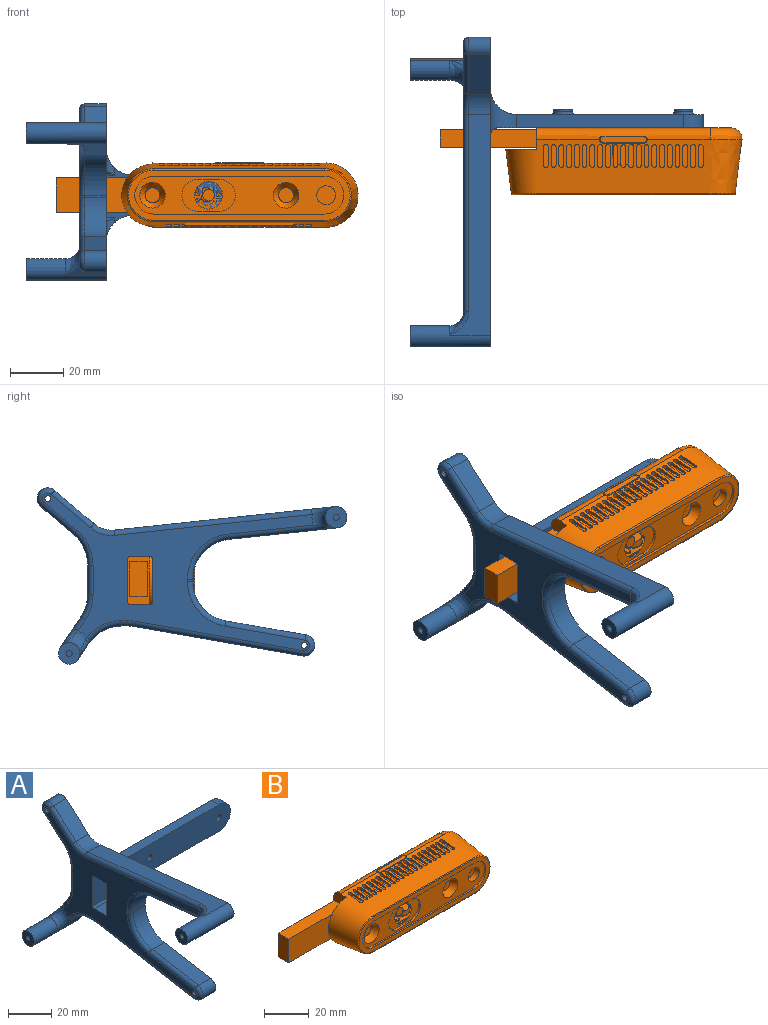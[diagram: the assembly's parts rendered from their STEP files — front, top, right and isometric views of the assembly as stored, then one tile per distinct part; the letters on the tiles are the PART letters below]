
ASSEMBLY  parts=2 mates=1
PART A: 85 faces, bbox 112.3x118.8x72.5 mm
  f0: plane 26.04x23.75mm, normal (1,0,0), area 153.5mm2, adj f2,f3,f4,f35,f36,f37,f38
  f1: plane 8x2.06mm, normal (0,0,-1), area 16.5mm2, adj f36,f37,f39,f75
  f2: plane 15.08x5.93mm, normal (0,-0.83,-0.56), area 75.7mm2, adj f0,f3,f37,f72
  f3: cylinder r=4mm len=30mm, axis (1,0,0), area 377mm2, adj f0,f2,f4,f48,f49
  f4: plane 15.08x11.42mm, normal (0,0.83,0.56), area 128.8mm2, adj f0,f3,f38,f70,f71
  f5: plane 11.07x8mm, normal (0,1,0), area 88.6mm2, adj f35,f38,f41,f68
  f6: plane 12.25x10.4mm, normal (0,0.65,-0.76), area 128.6mm2, adj f7,f21,f41,f66
  f7: cylinder r=4mm len=8mm, axis (1,0,0), area 100.5mm2, adj f6,f8,f21,f65
  f8: plane 14.75x12.52mm, normal (0,-0.65,0.76), area 154.8mm2, adj f7,f21,f60,f64
  f9: plane 85.19x17.55mm, normal (0,0.11,0.99), area 684mm2, adj f10,f21,f60,f61,f62
  f10: cylinder r=4mm len=30mm, axis (1,0,0), area 564.5mm2, adj f9,f11,f21,f47,f58
  f11: plane 40.7x15.08mm, normal (0,-0.11,-0.99), area 346mm2, adj f10,f21,f42,f83,f84
  f12: plane 8x0.82mm, normal (0,-1,0), area 6.6mm2, adj f21,f40,f42,f81
  f13: plane 29.98x8mm, normal (0,-0.17,0.99), area 243.5mm2, adj f14,f21,f40,f79
  f14: cylinder r=4mm len=8mm, axis (1,0,0), area 100.5mm2, adj f13,f19,f21,f78
  f15: plane 10.76x7.35mm, normal (0,0,-1), area 74mm2, adj f20,f21,f44,f56,f57
  f16: plane 89.86x20.72mm, normal (0,-1,0), area 1330mm2, adj f20,f22,f24,f25,f26,f30,f34,f36
  f17: plane 10.76x7.35mm, normal (0,0,1), area 74mm2, adj f20,f21,f43,f54,f55
  f18: plane 16x10mm, normal (0,1,0), area 160mm2, adj f20,f21,f55,f56
  f19: plane 62.91x11.02mm, normal (0,0.17,-0.99), area 511mm2, adj f14,f21,f39,f77
  f20: plane 101.4x59mm, normal (-1,0,0), area 1644.5mm2, adj f15,f16,f17,f18,f45,f46,f54,f55
  f21: plane 116x63mm, normal (1,0,0), area 1845mm2, adj f6,f7,f8,f9,f10,f11,f12,f13
  f22: plane 62.36x5mm, normal (0,0,1), area 311.8mm2, adj f16,f23,f24,f34
  f23: plane 69.86x15mm, normal (0,1,0), area 896.6mm2, adj f22,f24,f25,f32,f33,f35
  f24: cylinder r=7.5mm len=15mm, axis (0,1,0), area 117.8mm2, adj f16,f22,f23,f25
  f25: plane 62.36x5mm, normal (0,0,-1), area 311.8mm2, adj f16,f23,f24,f36
  f26: cylinder r=1.75mm len=7mm, axis (0,-1,0), area 77mm2, adj f16,f28
  f27: cylinder r=3.5mm len=7mm, axis (0,-1,0), area 22mm2, adj f28,f33
  f28: plane 7x7mm, normal (0,1,0), area 28.9mm2, adj f26,f27
  f29: cylinder r=3.5mm len=7mm, axis (0,-1,0), area 22mm2, adj f31,f32
  f30: cylinder r=1.75mm len=7mm, axis (0,-1,0), area 77mm2, adj f16,f31
  f31: plane 7x7mm, normal (0,1,0), area 28.9mm2, adj f29,f30
  f32: torus R=4.5mm, axis (0,1,0), area 38.1mm2, adj f23,f29
  f33: torus R=4.5mm, axis (0,1,0), area 38.1mm2, adj f23,f27
  f34: cylinder r=10mm len=18mm, axis (0,-1,0), area 169mm2, adj f16,f21,f22,f35,f44
  f35: cylinder r=10mm len=35mm, axis (0,0,1), area 392.7mm2, adj f0,f5,f21,f23,f34,f36
  f36: cylinder r=10mm len=18mm, axis (0,1,0), area 147.6mm2, adj f0,f1,f16,f21,f25,f35,f43
  f37: cylinder r=15mm len=12.44mm, axis (-1,0,0), area 117.4mm2, adj f0,f1,f2,f73,f74
  f38: cylinder r=15mm len=8.39mm, axis (-1,0,0), area 71.2mm2, adj f0,f4,f5,f69
  f39: cylinder r=15mm len=8mm, axis (-1,0,0), area 20.8mm2, adj f1,f19,f21,f76
  f40: cylinder r=15mm len=14.78mm, axis (1,0,0), area 167.7mm2, adj f12,f13,f21,f80
  f41: cylinder r=15mm len=11.43mm, axis (-1,0,0), area 104mm2, adj f5,f6,f21,f67
  f42: cylinder r=15mm len=14.92mm, axis (-1,0,0), area 175.8mm2, adj f11,f12,f21,f82
  f43: cylinder r=3mm len=9mm, axis (0,0,-1), area 22.1mm2, adj f16,f17,f21,f36,f54
  f44: cylinder r=3mm len=10mm, axis (0,0,-1), area 26.8mm2, adj f15,f16,f21,f34,f57
  f45: cylinder r=1.15mm len=10mm, axis (-1,0,0), area 72.3mm2, adj f20,f21
  f46: cylinder r=1.15mm len=10mm, axis (-1,0,0), area 72.3mm2, adj f20,f21
  f47: plane 8x8mm, normal (-1,0,0), area 46.1mm2, adj f10,f52
  f48: extruded ~14.92x7.32mm, area 187.5mm2, adj f3,f49,f59
  f49: plane 8x8mm, normal (-1,0,0), area 46.1mm2, adj f3,f48,f50
  f50: cylinder r=1.15mm len=7mm, axis (-1,0,0), area 50.6mm2, adj f49,f51
  f51: plane 2.3x2.3mm, normal (-1,0,0), area 4.2mm2, adj f50
  f52: cylinder r=1.15mm len=7mm, axis (-1,0,0), area 50.6mm2, adj f47,f53
  f53: plane 2.3x2.3mm, normal (-1,0,0), area 4.2mm2, adj f52
  f54: cylinder r=1mm len=13mm, axis (1,0,0), area 18.7mm2, adj f16,f17,f20,f43
  f55: cylinder r=1mm len=10mm, axis (-1,0,0), area 15.7mm2, adj f17,f18,f20,f21
  f56: cylinder r=1mm len=10mm, axis (-1,0,0), area 15.7mm2, adj f15,f18,f20,f21
  f57: cylinder r=1mm len=13mm, axis (1,0,0), area 18.7mm2, adj f15,f16,f20,f44
  f58: torus R=9.08mm, axis (1,0,0), area 51.8mm2, adj f10,f20,f61,f84
  f59: bspline ~16.86x14.51mm, area 51.9mm2, adj f20,f48,f71,f72,f73
  f60: cylinder r=10mm len=8mm, axis (-1,0,0), area 64.8mm2, adj f8,f9,f21,f63
  f61: bspline ~10.33x7.08mm, area 13.1mm2, adj f9,f58,f62
  f62: cylinder r=2mm len=74.12mm, axis (0,0.99,-0.11), area 233.5mm2, adj f9,f20,f61,f63
  f63: torus R=12mm, axis (1,0,0), area 27.3mm2, adj f20,f60,f62,f64
  f64: cylinder r=2mm len=16.04mm, axis (0,0.76,0.65), area 60.8mm2, adj f8,f20,f63,f65
  f65: torus R=2mm, axis (1,0,0), area 32.3mm2, adj f7,f20,f64,f66
  f66: cylinder r=2mm len=13.54mm, axis (0,-0.76,-0.65), area 50.5mm2, adj f6,f20,f65,f67
  f67: torus R=17mm, axis (1,0,0), area 42.8mm2, adj f20,f41,f66,f68
  f68: cylinder r=2mm len=11.07mm, axis (0,0,-1), area 34.8mm2, adj f5,f20,f67,f69
  f69: torus R=17mm, axis (1,0,0), area 29.3mm2, adj f20,f38,f68,f70
  f70: cylinder r=2mm len=5.19mm, axis (0,0.56,-0.83), area 15.4mm2, adj f4,f20,f69,f71
  f71: bspline ~8.69x7.34mm, area 22.2mm2, adj f4,f59,f70
  f72: bspline ~8.43x7.09mm, area 17.8mm2, adj f2,f59,f73
  f73: bspline ~3.5x3.18mm, area 4mm2, adj f37,f59,f72,f74
  f74: torus R=17mm, axis (1,0,0), area 43.4mm2, adj f20,f37,f73,f75
  f75: cylinder r=2mm len=2.06mm, axis (0,-1,0), area 6.5mm2, adj f1,f20,f74,f76
  f76: torus R=17mm, axis (1,0,0), area 8.6mm2, adj f20,f39,f75,f77
  f77: cylinder r=2mm len=63.26mm, axis (0,-0.99,-0.17), area 200.7mm2, adj f19,f20,f76,f78
  f78: torus R=2mm, axis (1,0,0), area 32.3mm2, adj f14,f20,f77,f79
  f79: cylinder r=2mm len=30.32mm, axis (0,0.99,0.17), area 95.6mm2, adj f13,f20,f78,f80
  f80: torus R=17mm, axis (1,0,0), area 69mm2, adj f20,f40,f79,f81
  f81: cylinder r=2mm len=2mm, axis (0,0,1), area 2.6mm2, adj f12,f20,f80,f82
  f82: torus R=17mm, axis (1,0,0), area 72.4mm2, adj f20,f42,f81,f83
  f83: cylinder r=2mm len=32.11mm, axis (0,-0.99,0.11), area 100.8mm2, adj f11,f20,f82,f84
  f84: bspline ~10.33x7.08mm, area 14mm2, adj f11,f58,f83
PART B: 273 faces, bbox 115x26.6x26.5 mm
  f0: plane 72.95x16.11mm, normal (0,1,0), area 1039mm2, adj f1,f2,f3,f5,f7,f8,f9,f10
  f1: plane 5.43x3.53mm, normal (0,1,0), area 10.2mm2, adj f0
  f2: plane 5.56x3.6mm, normal (0,1,0), area 10mm2, adj f0
  f3: plane 5.43x3.66mm, normal (0,1,0), area 10.5mm2, adj f0,f4
  f4: plane 1.8x1.17mm, normal (0,1,0), area 1.1mm2, adj f3
  f5: plane 5.29x4.21mm, normal (0,1,0), area 12.9mm2, adj f0,f6
  f6: plane 3.39x2.31mm, normal (0,1,0), area 6.8mm2, adj f5
  f7: plane 5.29x2.44mm, normal (0,1,0), area 6.4mm2, adj f0
  f8: plane 5.29x2.85mm, normal (0,1,0), area 10.4mm2, adj f0
  f9: plane 5.29x2.85mm, normal (0,1,0), area 6.8mm2, adj f0
  f10: plane 5.29x4.21mm, normal (0,1,0), area 13.9mm2, adj f0
  f11: plane 5.29x0.95mm, normal (0,1,0), area 5mm2, adj f0
  f12: bspline ~88.8x24.06mm, area 3050.5mm2, adj f13,f14,f16,f23,f24,f25,f45,f48
  f13: plane 8.47x8.17mm, normal (0,-0.11,0.99), area 24.1mm2, adj f12,f43,f44,f45,f46,f73,f74,f76
  f14: plane 11.2x9.5mm, normal (0,-0.11,-0.99), area 30.1mm2, adj f12,f25,f163
  f15: cylinder r=1.3mm len=0.93mm, axis (0,0,1), area 0mm2, adj f23,f149,f158
  f16: cylinder r=1.3mm len=1.3mm, axis (0,0,1), area 0.1mm2, adj f12,f151,f157
  f17: plane 78.22x14.12mm, normal (0,-1,0), area 668.8mm2, adj f26,f27,f28,f29,f31,f33,f34,f35
  f18: plane 82.93x18.8mm, normal (0,-1,0), area 421.2mm2, adj f26,f27,f28,f29,f245,f246,f247,f248
  f19: cylinder r=1.5mm len=3mm, axis (0,1,0), area 28.3mm2, adj f0,f20
  f20: plane 3x3mm, normal (0,1,0), area 7.1mm2, adj f19
  f21: cylinder r=1.5mm len=3mm, axis (0,1,0), area 28.3mm2, adj f0,f22
  f22: plane 3x3mm, normal (0,1,0), area 7.1mm2, adj f21
  f23: bspline ~65x4.42mm, area 413mm2, adj f0,f12,f15,f24,f148,f149,f156,f161
  f24: bspline ~25x12.86mm, area 226mm2, adj f0,f12,f23,f25
  f25: bspline ~66.76x4.5mm, area 435.6mm2, adj f0,f12,f14,f24,f266
  f26: cylinder r=7.06mm len=14.12mm, axis (0,-1,0), area 22.2mm2, adj f17,f18,f27,f29
  f27: plane 64.1x1mm, normal (0,0,-1), area 64.1mm2, adj f17,f18,f26,f28
  f28: cylinder r=7.06mm len=14.12mm, axis (0,-1,0), area 22.2mm2, adj f17,f18,f27,f29
  f29: plane 64.1x1mm, normal (0,0,1), area 64.1mm2, adj f17,f18,f26,f28
  f30: plane 5.59x5.59mm, normal (0,-1,0), area 24.5mm2, adj f31
  f31: revolved ~9.57x9.57mm, area 89.7mm2, adj f17,f30
  f32: plane 5.59x5.59mm, normal (0,-1,0), area 24.5mm2, adj f33
  f33: cone r=2.8mm half-angle=32.3deg, axis (0,-1,0), area 90.6mm2, adj f17,f32
  f34: plane 8x1.1mm, normal (0,0,-1), area 8.8mm2, adj f17,f35,f37,f38
  f35: cylinder r=6mm len=12mm, axis (0,-1,0), area 20.7mm2, adj f17,f34,f36,f38
  f36: plane 8x1.1mm, normal (0,0,1), area 8.8mm2, adj f17,f35,f37,f38
  f37: cylinder r=6mm len=12mm, axis (0,-1,0), area 20.7mm2, adj f17,f34,f36,f38
  f38: plane 20x12mm, normal (0,-1,0), area 124.5mm2, adj f34,f35,f36,f37,f40
  f39: plane 4.39x4.39mm, normal (0,-1,0), area 15.1mm2, adj f40
  f40: revolved ~10.38x10.38mm, area 168.9mm2, adj f38,f39
  f41: cylinder r=3.5mm len=7mm, axis (0,-1,0), area 70.4mm2, adj f17,f42
  f42: plane 7x7mm, normal (0,-1,0), area 38.5mm2, adj f41
  f43: cylinder r=0.9mm len=1.8mm, axis (0,0,1), area 4mm2, adj f13,f44,f46,f47
  f44: plane 6.7x1.41mm, normal (-1,0,0), area 7.1mm2, adj f13,f43,f45,f47
  f45: cylinder r=0.9mm len=1.8mm, axis (0,0,1), area 1.8mm2, adj f12,f13,f44,f46,f47
  f46: plane 6.7x1.41mm, normal (1,0,0), area 7.1mm2, adj f13,f43,f45,f47
  f47: plane 8.5x1.8mm, normal (0,0,1), area 14.6mm2, adj f43,f44,f45,f46
  f48: cylinder r=0.9mm len=1.8mm, axis (0,0,1), area 4mm2, adj f12,f49,f51,f52
  f49: plane 6.7x1.41mm, normal (-1,0,0), area 7.1mm2, adj f12,f48,f50,f52
  f50: cylinder r=0.9mm len=1.8mm, axis (0,0,1), area 2mm2, adj f12,f49,f51,f52
  f51: plane 6.7x1.41mm, normal (1,0,0), area 7.1mm2, adj f12,f48,f50,f52
  f52: plane 8.5x1.8mm, normal (0,0,1), area 14.6mm2, adj f48,f49,f50,f51
  f53: cylinder r=0.9mm len=1.8mm, axis (0,0,1), area 4mm2, adj f12,f54,f56,f57
  f54: plane 6.7x1.41mm, normal (-1,0,0), area 7.1mm2, adj f12,f53,f55,f57
  f55: cylinder r=0.9mm len=1.8mm, axis (0,0,1), area 2mm2, adj f12,f54,f56,f57
  f56: plane 6.7x1.41mm, normal (1,0,0), area 7.1mm2, adj f12,f53,f55,f57
  f57: plane 8.5x1.8mm, normal (0,0,1), area 14.6mm2, adj f53,f54,f55,f56
  f58: cylinder r=0.9mm len=1.8mm, axis (0,0,1), area 4mm2, adj f12,f59,f61,f62
  f59: plane 6.7x1.41mm, normal (-1,0,0), area 7.1mm2, adj f12,f58,f60,f62
  f60: cylinder r=0.9mm len=1.8mm, axis (0,0,1), area 2mm2, adj f12,f59,f61,f62
  f61: plane 6.7x1.41mm, normal (1,0,0), area 7.1mm2, adj f12,f58,f60,f62
  f62: plane 8.5x1.8mm, normal (0,0,1), area 14.6mm2, adj f58,f59,f60,f61
  f63: cylinder r=0.9mm len=1.8mm, axis (0,0,1), area 4mm2, adj f12,f64,f66,f67
  f64: plane 6.7x1.41mm, normal (-1,0,0), area 7.1mm2, adj f12,f63,f65,f67
  f65: cylinder r=0.9mm len=1.8mm, axis (0,0,1), area 2mm2, adj f12,f64,f66,f67
  f66: plane 6.7x1.41mm, normal (1,0,0), area 7.1mm2, adj f12,f63,f65,f67
  f67: plane 8.5x1.8mm, normal (0,0,1), area 14.6mm2, adj f63,f64,f65,f66
  f68: cylinder r=0.9mm len=1.8mm, axis (0,0,1), area 4mm2, adj f12,f69,f71,f72
  f69: plane 6.7x1.41mm, normal (-1,0,0), area 7.1mm2, adj f12,f68,f70,f72
  f70: cylinder r=0.9mm len=1.8mm, axis (0,0,1), area 2mm2, adj f12,f69,f71,f72
  f71: plane 6.7x1.41mm, normal (1,0,0), area 7.1mm2, adj f12,f68,f70,f72
  f72: plane 8.5x1.8mm, normal (0,0,1), area 14.6mm2, adj f68,f69,f70,f71
  f73: cylinder r=0.9mm len=1.8mm, axis (0,0,1), area 4mm2, adj f13,f74,f76,f77
  f74: plane 6.7x1.41mm, normal (-1,0,0), area 7.1mm2, adj f12,f13,f73,f75,f77
  f75: cylinder r=0.9mm len=1.8mm, axis (0,0,1), area 2mm2, adj f12,f74,f76,f77
  f76: plane 6.7x1.41mm, normal (1,0,0), area 7.1mm2, adj f12,f13,f73,f75,f77
  f77: plane 8.5x1.8mm, normal (0,0,1), area 14.6mm2, adj f73,f74,f75,f76
  f78: cylinder r=0.9mm len=1.8mm, axis (0,0,1), area 4mm2, adj f12,f79,f81,f82
  f79: plane 6.7x1.41mm, normal (-1,0,0), area 7.1mm2, adj f12,f78,f80,f82
  f80: cylinder r=0.9mm len=1.8mm, axis (0,0,1), area 2mm2, adj f12,f79,f81,f82
  f81: plane 6.7x1.41mm, normal (1,0,0), area 7.1mm2, adj f12,f78,f80,f82
  f82: plane 8.5x1.8mm, normal (0,0,1), area 14.6mm2, adj f78,f79,f80,f81
  f83: cylinder r=0.9mm len=1.8mm, axis (0,0,1), area 4mm2, adj f12,f84,f86,f87
  f84: plane 6.7x1.41mm, normal (-1,0,0), area 7.1mm2, adj f12,f83,f85,f87
  f85: cylinder r=0.9mm len=1.8mm, axis (0,0,1), area 2mm2, adj f12,f84,f86,f87
  f86: plane 6.7x1.41mm, normal (1,0,0), area 7.1mm2, adj f12,f83,f85,f87
  f87: plane 8.5x1.8mm, normal (0,0,1), area 14.6mm2, adj f83,f84,f85,f86
  f88: cylinder r=0.9mm len=1.8mm, axis (0,0,1), area 4mm2, adj f12,f89,f91,f92
  f89: plane 6.7x1.41mm, normal (-1,0,0), area 7.1mm2, adj f12,f88,f90,f92
  f90: cylinder r=0.9mm len=1.8mm, axis (0,0,1), area 2mm2, adj f12,f89,f91,f92
  f91: plane 6.7x1.41mm, normal (1,0,0), area 7.1mm2, adj f12,f88,f90,f92
  f92: plane 8.5x1.8mm, normal (0,0,1), area 14.6mm2, adj f88,f89,f90,f91
  f93: cylinder r=0.9mm len=1.8mm, axis (0,0,1), area 4mm2, adj f12,f94,f96,f97
  f94: plane 6.7x1.41mm, normal (-1,0,0), area 7.1mm2, adj f12,f93,f95,f97
  f95: cylinder r=0.9mm len=1.8mm, axis (0,0,1), area 2mm2, adj f12,f94,f96,f97
  f96: plane 6.7x1.41mm, normal (1,0,0), area 7.1mm2, adj f12,f93,f95,f97
  f97: plane 8.5x1.8mm, normal (0,0,1), area 14.6mm2, adj f93,f94,f95,f96
  f98: cylinder r=0.9mm len=1.8mm, axis (0,0,1), area 4mm2, adj f12,f99,f101,f102
  f99: plane 6.7x1.41mm, normal (-1,0,0), area 7.1mm2, adj f12,f98,f100,f102
  f100: cylinder r=0.9mm len=1.8mm, axis (0,0,1), area 2mm2, adj f12,f99,f101,f102
  f101: plane 6.7x1.41mm, normal (1,0,0), area 7.1mm2, adj f12,f98,f100,f102
  f102: plane 8.5x1.8mm, normal (0,0,1), area 14.6mm2, adj f98,f99,f100,f101
  f103: cylinder r=0.9mm len=1.8mm, axis (0,0,1), area 4mm2, adj f12,f104,f106,f107
  f104: plane 6.7x1.41mm, normal (-1,0,0), area 7.1mm2, adj f12,f103,f105,f107
  f105: cylinder r=0.9mm len=1.8mm, axis (0,0,1), area 2mm2, adj f12,f104,f106,f107
  f106: plane 6.7x1.41mm, normal (1,0,0), area 7.1mm2, adj f12,f103,f105,f107
  f107: plane 8.5x1.8mm, normal (0,0,1), area 14.6mm2, adj f103,f104,f105,f106
  f108: cylinder r=0.9mm len=1.8mm, axis (0,0,1), area 4mm2, adj f12,f109,f111,f112
  f109: plane 6.7x1.41mm, normal (-1,0,0), area 7.1mm2, adj f12,f108,f110,f112
  f110: cylinder r=0.9mm len=1.8mm, axis (0,0,1), area 2mm2, adj f12,f109,f111,f112
  f111: plane 6.7x1.41mm, normal (1,0,0), area 7.1mm2, adj f12,f108,f110,f112
  f112: plane 8.5x1.8mm, normal (0,0,1), area 14.6mm2, adj f108,f109,f110,f111
  f113: cylinder r=0.9mm len=1.8mm, axis (0,0,1), area 4mm2, adj f12,f114,f116,f117
  f114: plane 6.7x1.41mm, normal (-1,0,0), area 7.1mm2, adj f12,f113,f115,f117
  f115: cylinder r=0.9mm len=1.8mm, axis (0,0,1), area 2mm2, adj f12,f114,f116,f117
  f116: plane 6.7x1.41mm, normal (1,0,0), area 7.1mm2, adj f12,f113,f115,f117
  f117: plane 8.5x1.8mm, normal (0,0,1), area 14.6mm2, adj f113,f114,f115,f116
  f118: cylinder r=0.9mm len=1.8mm, axis (0,0,1), area 4mm2, adj f12,f119,f121,f122
  f119: plane 6.7x1.41mm, normal (-1,0,0), area 7.1mm2, adj f12,f118,f120,f122
  f120: cylinder r=0.9mm len=1.8mm, axis (0,0,1), area 2mm2, adj f12,f119,f121,f122
  f121: plane 6.7x1.41mm, normal (1,0,0), area 7.1mm2, adj f12,f118,f120,f122
  f122: plane 8.5x1.8mm, normal (0,0,1), area 14.6mm2, adj f118,f119,f120,f121
  f123: cylinder r=0.9mm len=1.8mm, axis (0,0,1), area 4mm2, adj f13,f124,f126,f127
  f124: plane 6.7x1.41mm, normal (-1,0,0), area 7.1mm2, adj f12,f13,f123,f125,f127
  f125: cylinder r=0.9mm len=1.8mm, axis (0,0,1), area 2mm2, adj f12,f124,f126,f127
  f126: plane 6.7x1.41mm, normal (1,0,0), area 7.1mm2, adj f12,f13,f123,f125,f127
  f127: plane 8.5x1.8mm, normal (0,0,1), area 14.6mm2, adj f123,f124,f125,f126
  f128: cylinder r=0.9mm len=1.8mm, axis (0,0,1), area 4mm2, adj f12,f129,f131,f132
  f129: plane 6.7x1.41mm, normal (-1,0,0), area 7.1mm2, adj f12,f128,f130,f132
  f130: cylinder r=0.9mm len=1.8mm, axis (0,0,1), area 2mm2, adj f12,f129,f131,f132
  f131: plane 6.7x1.41mm, normal (1,0,0), area 7.1mm2, adj f12,f128,f130,f132
  f132: plane 8.5x1.8mm, normal (0,0,1), area 14.6mm2, adj f128,f129,f130,f131
  f133: cylinder r=0.9mm len=1.8mm, axis (0,0,1), area 4mm2, adj f12,f134,f136,f137
  f134: plane 6.7x1.41mm, normal (-1,0,0), area 7.1mm2, adj f12,f133,f135,f137
  f135: cylinder r=0.9mm len=1.8mm, axis (0,0,1), area 2mm2, adj f12,f134,f136,f137
  f136: plane 6.7x1.41mm, normal (1,0,0), area 7.1mm2, adj f12,f133,f135,f137
  f137: plane 8.5x1.8mm, normal (0,0,1), area 14.6mm2, adj f133,f134,f135,f136
  f138: cylinder r=0.9mm len=1.8mm, axis (0,0,1), area 4mm2, adj f12,f139,f141,f142
  f139: plane 6.7x1.41mm, normal (-1,0,0), area 7.1mm2, adj f12,f138,f140,f142
  f140: cylinder r=0.9mm len=1.8mm, axis (0,0,1), area 2mm2, adj f12,f139,f141,f142
  f141: plane 6.7x1.41mm, normal (1,0,0), area 7.1mm2, adj f12,f138,f140,f142
  f142: plane 8.5x1.8mm, normal (0,0,1), area 14.6mm2, adj f138,f139,f140,f141
  f143: cylinder r=0.9mm len=1.8mm, axis (0,0,1), area 4mm2, adj f12,f144,f146,f147
  f144: plane 6.7x1.41mm, normal (-1,0,0), area 7.1mm2, adj f12,f143,f145,f147
  f145: cylinder r=0.9mm len=1.8mm, axis (0,0,1), area 2mm2, adj f12,f144,f146,f147
  f146: plane 6.7x1.41mm, normal (1,0,0), area 7.1mm2, adj f12,f143,f145,f147
  f147: plane 8.5x1.8mm, normal (0,0,1), area 14.6mm2, adj f143,f144,f145,f146
  f148: cylinder r=1.3mm len=0.93mm, axis (0,0,1), area 0mm2, adj f23,f149,f162
  f149: plane 15.24x0.07mm, normal (0,1,0), area 1mm2, adj f15,f23,f148,f160
  f150: cylinder r=1.3mm len=1.3mm, axis (0,0,1), area 0.1mm2, adj f12,f151,f153
  f151: plane 15.24x0.13mm, normal (0,-1,0), area 2mm2, adj f12,f13,f16,f150,f155
  f152: plane 17.44x2.2mm, normal (0,0,1), area 37.3mm2, adj f153,f154,f155,f156,f157,f158,f159,f160
  f153: torus R=1.1mm, axis (0,0,1), area 0.6mm2, adj f150,f152,f154,f155
  f154: bspline ~0.44x0.25mm, area 0mm2, adj f12,f152,f153,f156
  f155: cylinder r=0.2mm len=15.24mm, axis (1,0,0), area 4.8mm2, adj f151,f152,f153,f157
  f156: bspline ~1.2x0.63mm, area 0.3mm2, adj f23,f152,f154,f158
  f157: torus R=1.1mm, axis (0,0,1), area 0.6mm2, adj f16,f152,f155,f159
  f158: torus R=1.1mm, axis (0,0,1), area 0.3mm2, adj f15,f152,f156,f160
  f159: bspline ~0.42x0.23mm, area 0mm2, adj f12,f152,f157,f161
  f160: cylinder r=0.2mm len=15.24mm, axis (-1,0,0), area 4.8mm2, adj f149,f152,f158,f162
  f161: bspline ~1.19x0.65mm, area 0.3mm2, adj f23,f152,f159,f162
  f162: torus R=1.1mm, axis (0,0,1), area 0.3mm2, adj f148,f152,f160,f161
  f163: cylinder r=3.59mm len=7.18mm, axis (0,0,-1), area 74.1mm2, adj f14,f164
  f164: plane 7.18x7.18mm, normal (0,0,-1), area 40.5mm2, adj f163
  f165: cylinder r=0.9mm len=1.8mm, axis (0,0,-1), area 4mm2, adj f12,f166,f168,f169
  f166: plane 6.7x1.41mm, normal (1,0,0), area 7.1mm2, adj f12,f165,f167,f169
  f167: cylinder r=0.9mm len=1.8mm, axis (0,0,-1), area 2mm2, adj f12,f166,f168,f169
  f168: plane 6.7x1.41mm, normal (-1,0,0), area 7.1mm2, adj f12,f165,f167,f169
  f169: plane 8.5x1.8mm, normal (0,0,-1), area 14.6mm2, adj f165,f166,f167,f168
  f170: cylinder r=0.9mm len=1.8mm, axis (0,0,-1), area 4mm2, adj f12,f171,f173,f174
  f171: plane 6.7x1.41mm, normal (1,0,0), area 7.1mm2, adj f12,f170,f172,f174
  f172: cylinder r=0.9mm len=1.8mm, axis (0,0,-1), area 2mm2, adj f12,f171,f173,f174
  f173: plane 6.7x1.41mm, normal (-1,0,0), area 7.1mm2, adj f12,f170,f172,f174
  f174: plane 8.5x1.8mm, normal (0,0,-1), area 14.6mm2, adj f170,f171,f172,f173
  f175: cylinder r=0.9mm len=1.8mm, axis (0,0,-1), area 4mm2, adj f12,f176,f178,f179
  f176: plane 6.7x1.41mm, normal (1,0,0), area 7.1mm2, adj f12,f175,f177,f179
  f177: cylinder r=0.9mm len=1.8mm, axis (0,0,-1), area 2mm2, adj f12,f176,f178,f179
  f178: plane 6.7x1.41mm, normal (-1,0,0), area 7.1mm2, adj f12,f175,f177,f179
  f179: plane 8.5x1.8mm, normal (0,0,-1), area 14.6mm2, adj f175,f176,f177,f178
  f180: cylinder r=0.9mm len=1.8mm, axis (0,0,-1), area 4mm2, adj f12,f181,f183,f184
  f181: plane 6.7x1.41mm, normal (1,0,0), area 7.1mm2, adj f12,f180,f182,f184
  f182: cylinder r=0.9mm len=1.8mm, axis (0,0,-1), area 2mm2, adj f12,f181,f183,f184
  f183: plane 6.7x1.41mm, normal (-1,0,0), area 7.1mm2, adj f12,f180,f182,f184
  f184: plane 8.5x1.8mm, normal (0,0,-1), area 14.6mm2, adj f180,f181,f182,f183
  f185: cylinder r=0.9mm len=1.8mm, axis (0,0,-1), area 4mm2, adj f12,f186,f188,f189
  f186: plane 6.7x1.41mm, normal (1,0,0), area 7.1mm2, adj f12,f185,f187,f189
  f187: cylinder r=0.9mm len=1.8mm, axis (0,0,-1), area 2mm2, adj f12,f186,f188,f189
  f188: plane 6.7x1.41mm, normal (-1,0,0), area 7.1mm2, adj f12,f185,f187,f189
  f189: plane 8.5x1.8mm, normal (0,0,-1), area 14.6mm2, adj f185,f186,f187,f188
  f190: cylinder r=0.9mm len=1.8mm, axis (0,0,-1), area 4mm2, adj f12,f191,f193,f194
  f191: plane 6.7x1.41mm, normal (1,0,0), area 7.1mm2, adj f12,f190,f192,f194
  f192: cylinder r=0.9mm len=1.8mm, axis (0,0,-1), area 2mm2, adj f12,f191,f193,f194
  f193: plane 6.7x1.41mm, normal (-1,0,0), area 7.1mm2, adj f12,f190,f192,f194
  f194: plane 8.5x1.8mm, normal (0,0,-1), area 14.6mm2, adj f190,f191,f192,f193
  f195: cylinder r=0.9mm len=1.8mm, axis (0,0,-1), area 4mm2, adj f12,f196,f198,f199
  f196: plane 6.7x1.41mm, normal (1,0,0), area 7.1mm2, adj f12,f195,f197,f199
  f197: cylinder r=0.9mm len=1.8mm, axis (0,0,-1), area 2mm2, adj f12,f196,f198,f199
  f198: plane 6.7x1.41mm, normal (-1,0,0), area 7.1mm2, adj f12,f195,f197,f199
  f199: plane 8.5x1.8mm, normal (0,0,-1), area 14.6mm2, adj f195,f196,f197,f198
  f200: cylinder r=0.9mm len=1.8mm, axis (0,0,-1), area 4mm2, adj f12,f201,f203,f204
  f201: plane 6.7x1.41mm, normal (1,0,0), area 7.1mm2, adj f12,f200,f202,f204
  f202: cylinder r=0.9mm len=1.8mm, axis (0,0,-1), area 2mm2, adj f12,f201,f203,f204
  f203: plane 6.7x1.41mm, normal (-1,0,0), area 7.1mm2, adj f12,f200,f202,f204
  f204: plane 8.5x1.8mm, normal (0,0,-1), area 14.6mm2, adj f200,f201,f202,f203
  f205: cylinder r=0.9mm len=1.8mm, axis (0,0,-1), area 4mm2, adj f12,f206,f208,f209
  f206: plane 6.7x1.41mm, normal (1,0,0), area 7.1mm2, adj f12,f205,f207,f209
  f207: cylinder r=0.9mm len=1.8mm, axis (0,0,-1), area 2mm2, adj f12,f206,f208,f209
  f208: plane 6.7x1.41mm, normal (-1,0,0), area 7.1mm2, adj f12,f205,f207,f209
  f209: plane 8.5x1.8mm, normal (0,0,-1), area 14.6mm2, adj f205,f206,f207,f208
  f210: cylinder r=0.9mm len=1.8mm, axis (0,0,-1), area 4mm2, adj f12,f211,f213,f214
  f211: plane 6.7x1.41mm, normal (1,0,0), area 7.1mm2, adj f12,f210,f212,f214
  f212: cylinder r=0.9mm len=1.8mm, axis (0,0,-1), area 2mm2, adj f12,f211,f213,f214
  f213: plane 6.7x1.41mm, normal (-1,0,0), area 7.1mm2, adj f12,f210,f212,f214
  f214: plane 8.5x1.8mm, normal (0,0,-1), area 14.6mm2, adj f210,f211,f212,f213
  f215: cylinder r=0.9mm len=1.8mm, axis (0,0,-1), area 4mm2, adj f12,f216,f218,f219
  f216: plane 6.7x1.41mm, normal (1,0,0), area 7.1mm2, adj f12,f215,f217,f219
  f217: cylinder r=0.9mm len=1.8mm, axis (0,0,-1), area 2mm2, adj f12,f216,f218,f219
  f218: plane 6.7x1.41mm, normal (-1,0,0), area 7.1mm2, adj f12,f215,f217,f219
  f219: plane 8.5x1.8mm, normal (0,0,-1), area 14.6mm2, adj f215,f216,f217,f218
  f220: cylinder r=0.9mm len=1.8mm, axis (0,0,-1), area 4mm2, adj f12,f221,f223,f224
  f221: plane 6.7x1.41mm, normal (1,0,0), area 7.1mm2, adj f12,f220,f222,f224
  f222: cylinder r=0.9mm len=1.8mm, axis (0,0,-1), area 2mm2, adj f12,f221,f223,f224
  f223: plane 6.7x1.41mm, normal (-1,0,0), area 7.1mm2, adj f12,f220,f222,f224
  f224: plane 8.5x1.8mm, normal (0,0,-1), area 14.6mm2, adj f220,f221,f222,f223
  f225: cylinder r=0.9mm len=1.8mm, axis (0,0,-1), area 4mm2, adj f12,f226,f228,f229
  f226: plane 6.7x1.41mm, normal (1,0,0), area 7.1mm2, adj f12,f225,f227,f229
  f227: cylinder r=0.9mm len=1.8mm, axis (0,0,-1), area 2mm2, adj f12,f226,f228,f229
  f228: plane 6.7x1.41mm, normal (-1,0,0), area 7.1mm2, adj f12,f225,f227,f229
  f229: plane 8.5x1.8mm, normal (0,0,-1), area 14.6mm2, adj f225,f226,f227,f228
  f230: cylinder r=0.9mm len=1.8mm, axis (0,0,-1), area 4mm2, adj f12,f231,f233,f234
  f231: plane 6.7x1.41mm, normal (1,0,0), area 7.1mm2, adj f12,f230,f232,f234
  f232: cylinder r=0.9mm len=1.8mm, axis (0,0,-1), area 2mm2, adj f12,f231,f233,f234
  f233: plane 6.7x1.41mm, normal (-1,0,0), area 7.1mm2, adj f12,f230,f232,f234
  f234: plane 8.5x1.8mm, normal (0,0,-1), area 14.6mm2, adj f230,f231,f232,f233
  f235: cylinder r=0.9mm len=1.8mm, axis (0,0,-1), area 4mm2, adj f12,f236,f238,f239
  f236: plane 6.7x1.41mm, normal (1,0,0), area 7.1mm2, adj f12,f235,f237,f239
  f237: cylinder r=0.9mm len=1.8mm, axis (0,0,-1), area 2mm2, adj f12,f236,f238,f239
  f238: plane 6.7x1.41mm, normal (-1,0,0), area 7.1mm2, adj f12,f235,f237,f239
  f239: plane 8.5x1.8mm, normal (0,0,-1), area 14.6mm2, adj f235,f236,f237,f238
  f240: cylinder r=0.9mm len=1.8mm, axis (0,0,-1), area 4mm2, adj f12,f241,f243,f244
  f241: plane 6.7x1.41mm, normal (1,0,0), area 7.1mm2, adj f12,f240,f242,f244
  f242: cylinder r=0.9mm len=1.8mm, axis (0,0,-1), area 2mm2, adj f12,f241,f243,f244
  f243: plane 6.7x1.41mm, normal (-1,0,0), area 7.1mm2, adj f12,f240,f242,f244
  f244: plane 8.5x1.8mm, normal (0,0,-1), area 14.6mm2, adj f240,f241,f242,f243
  f245: bspline ~45.29x19.79mm, area 22.2mm2, adj f12,f18,f246,f247
  f246: bspline ~64.1x0.5mm, area 47mm2, adj f12,f18,f245,f248
  f247: bspline ~64.1x0.5mm, area 47mm2, adj f12,f18,f245,f248
  f248: bspline ~19.79x9.9mm, area 22.2mm2, adj f12,f18,f246,f247
  f249: plane 3.72x0.93mm, normal (1,0,0), area 2.7mm2, adj f12,f254,f255,f264
  f250: plane 40.91x0.55mm, normal (0,1,0), area 20.9mm2, adj f12,f255,f256,f263
  f251: plane 3.72x0.93mm, normal (-1,0,0), area 2.7mm2, adj f12,f256,f257,f259
  f252: plane 40.87x0.95mm, normal (0,-1,0), area 38.7mm2, adj f12,f254,f257,f260
  f253: plane 40.87x3.72mm, normal (0,0,-1), area 152mm2, adj f259,f260,f263,f264
  f254: cylinder r=0.2mm len=0.95mm, axis (0,0,-1), area 0.3mm2, adj f12,f249,f252,f262
  f255: cylinder r=0.2mm len=0.53mm, axis (0,0,-1), area 0.2mm2, adj f12,f249,f250,f265
  f256: cylinder r=0.2mm len=0.53mm, axis (0,0,-1), area 0.2mm2, adj f12,f250,f251,f261
  f257: cylinder r=0.2mm len=0.95mm, axis (0,0,-1), area 0.3mm2, adj f12,f251,f252,f258
  f258: sphere r=0.2mm, area 0.1mm2, adj f257,f259,f260
  f259: cylinder r=0.2mm len=3.72mm, axis (0,1,0), area 1.2mm2, adj f251,f253,f258,f261
  f260: cylinder r=0.2mm len=40.87mm, axis (-1,0,0), area 12.8mm2, adj f252,f253,f258,f262
  f261: sphere r=0.2mm, area 0.1mm2, adj f256,f259,f263
  f262: sphere r=0.2mm, area 0.1mm2, adj f254,f260,f264
  f263: cylinder r=0.2mm len=40.87mm, axis (1,0,0), area 12.8mm2, adj f250,f253,f261,f265
  f264: cylinder r=0.2mm len=3.72mm, axis (0,-1,0), area 1.2mm2, adj f249,f253,f262,f265
  f265: sphere r=0.2mm, area 0mm2, adj f255,f263,f264
  f266: plane 24.27x8.16mm, normal (-1,0,0), area 97.4mm2, adj f0,f12,f23,f25,f267,f268,f269,f270
  f267: plane 23.31x11.54mm, normal (0,1,0), area 210.6mm2, adj f12,f266
  f268: plane 36x6.7mm, normal (0,0,-1), area 241.2mm2, adj f266,f269,f271,f272
  f269: plane 36x13mm, normal (0,-1,0), area 468mm2, adj f266,f268,f270,f272
  f270: plane 36x6.7mm, normal (0,0,1), area 241.2mm2, adj f266,f269,f271,f272
  f271: plane 36x13mm, normal (0,1,0), area 468mm2, adj f266,f268,f270,f272
  f272: plane 13x6.7mm, normal (-1,0,0), area 87.1mm2, adj f268,f269,f270,f271
PLACE A t=(-12.11,10.77,-6.33)mm
PLACE B t=(-12.11,5.77,-6.33)mm
MATE cylindrical A.f30 <-> B.f21  axis (0,-1,0) through (10.39,5.77,-6.33)mm
